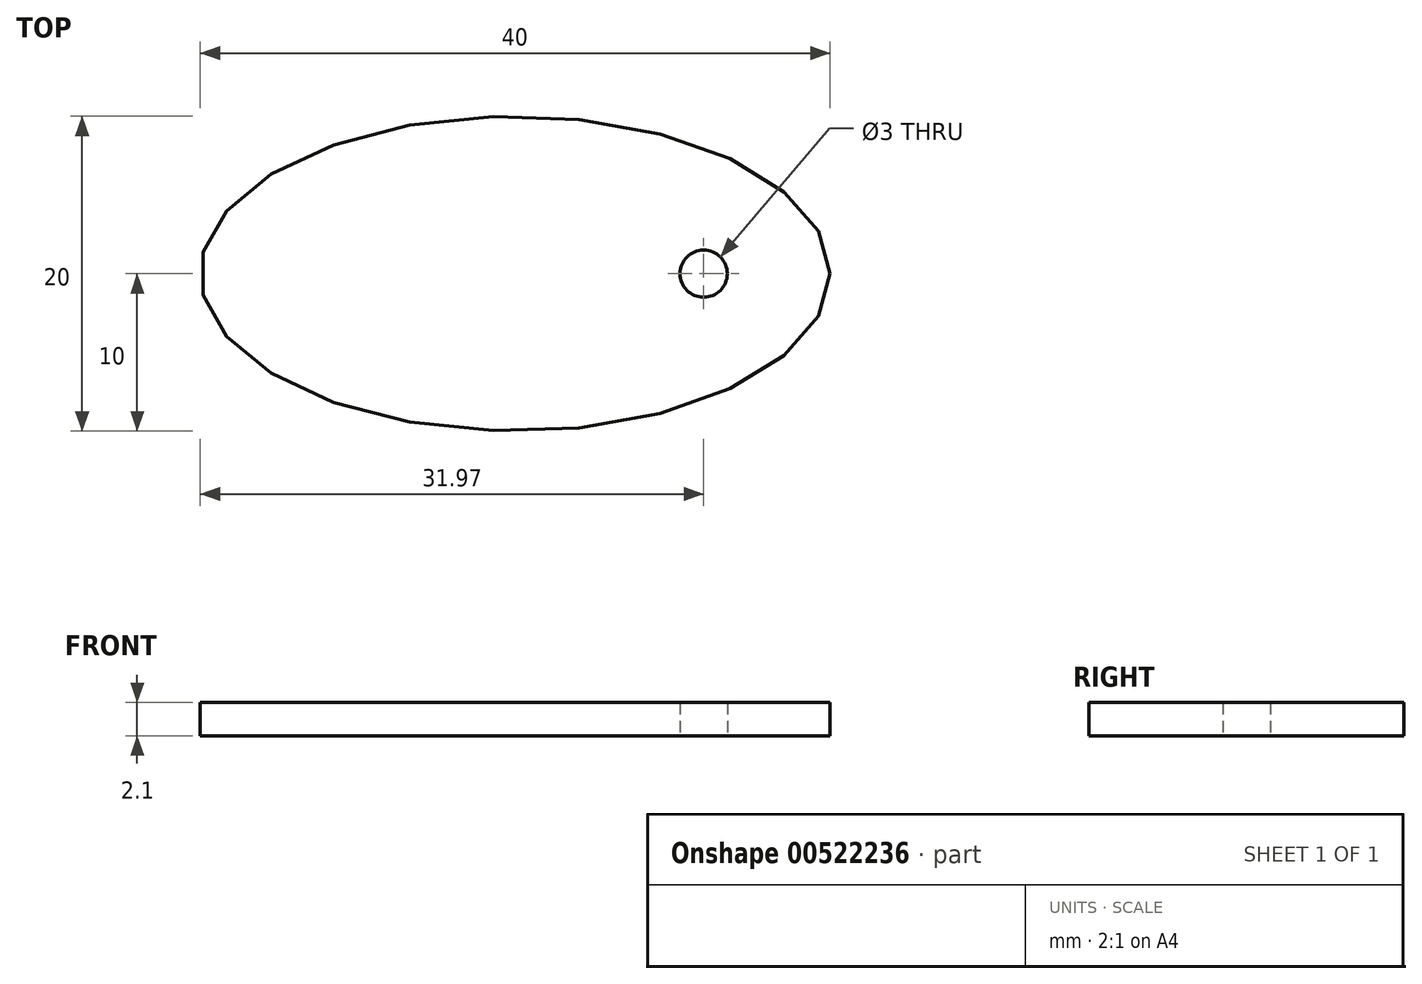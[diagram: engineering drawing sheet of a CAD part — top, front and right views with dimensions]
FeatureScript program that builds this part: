
annotation { "Feature Type Name" : "Feature", "Feature Type Description" : "" }
export const myFeature = defineFeature(function(context is Context, id is Id, definition is map)
    precondition{}
    {
        {
            var Q0;
            Q0=qCreatedBy(makeId("Top.planeOp"),FACE);
            var sketch = newSketch(context, id + "F0", { "sketchPlane" : qUnion([Q0])});
            skEllipse(sketch, "E0", {"center": v(-11.97, 0) * mm, "majorRadius": 20 * mm, "minorRadius": 10 * mm, "majorAxis": v(1, 0)});
            skPoint(sketch, "E1", {"position": v(0, 0) * mm});
            skCircle(sketch, "E2", {"center": v(0, 0) * mm, "radius": 1.5 * mm});
            skSolve(sketch);
        }
        {
            var Q0;
            Q0=makeQuery(id+"F0.imprint","IMPRINT",FACE,{"disambiguationData":[TD([[makeQuery(id+"F0.imprint","IMPRINT",EDGE,{"derivedFrom":sQuery(id+"F0.wireOp",EDGE,"E0")}),1.0]])]});
            extrude(context, id + "F1", {"entities" : qUnion([Q0]), "depth" : 2.1 * mm, "offsetDistance" : 25 * mm});
        }
    });
